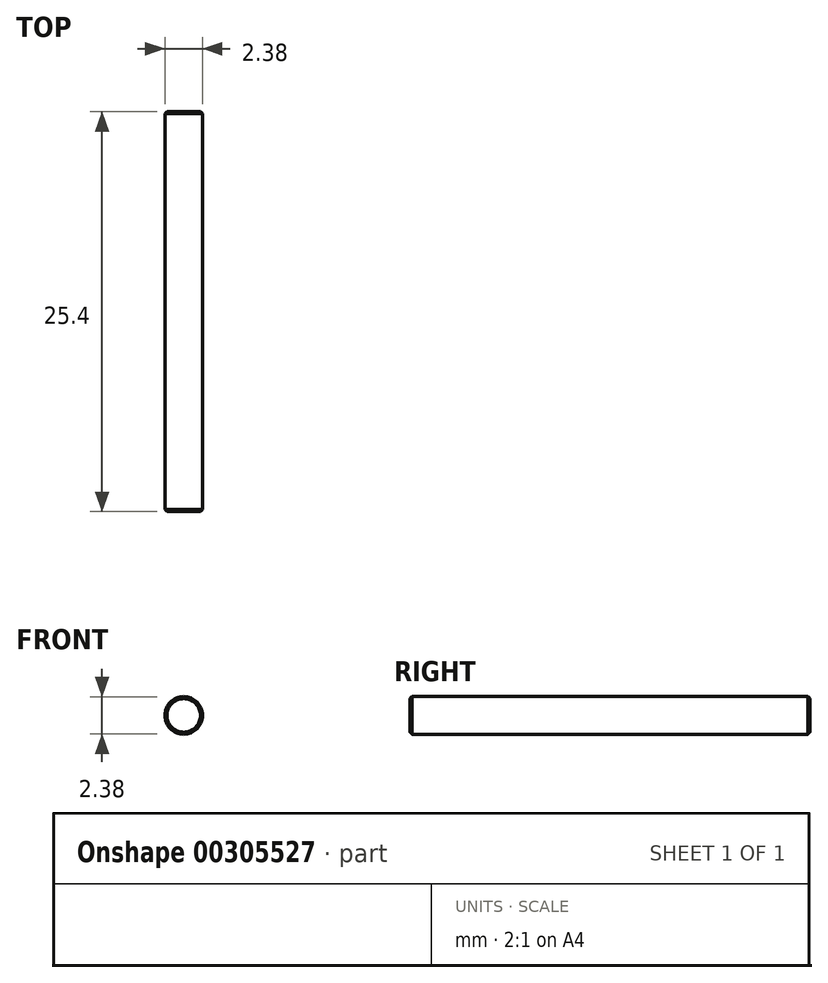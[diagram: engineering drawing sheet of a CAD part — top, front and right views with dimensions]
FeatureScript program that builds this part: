
annotation { "Feature Type Name" : "Feature", "Feature Type Description" : "" }
export const myFeature = defineFeature(function(context is Context, id is Id, definition is map)
    precondition{}
    {
        {
            var Q0;
            Q0=qCreatedBy(makeId("Front.planeOp"),FACE);
            var sketch = newSketch(context, id + "F0", { "sketchPlane" : qUnion([Q0])});
            skCircle(sketch, "E0", {"center": v(0, 0) * mm, "radius": 1.2 * mm});
            skSolve(sketch);
        }
        {
            var Q0;
            Q0 = qSketchRegion(id + "F0", true);
            extrude(context, id + "F1", {"entities" : qUnion([Q0]), "oppositeDirection" : true, "depth" : 25.4 * mm});
        }
        {
            var Q0;
            Q0=makeQuery(id+"F1.opExtrude","CAP_EDGE",EDGE,{"disambiguationData":[OSD([sQuery(id+"F0.wireOp",EDGE,"E0")])],"isStart":true});
            var Q1;
            Q1=makeQuery(id+"F1.opExtrude","CAP_EDGE",EDGE,{"disambiguationData":[OSD([sQuery(id+"F0.wireOp",EDGE,"E0")])],"isStart":false});
            chamfer(context, id + "F2", {"entities" : qUnion([Q0, Q1]), "width" : 0.13 * mm, "tangentPropagation" : true});
        }
    });
